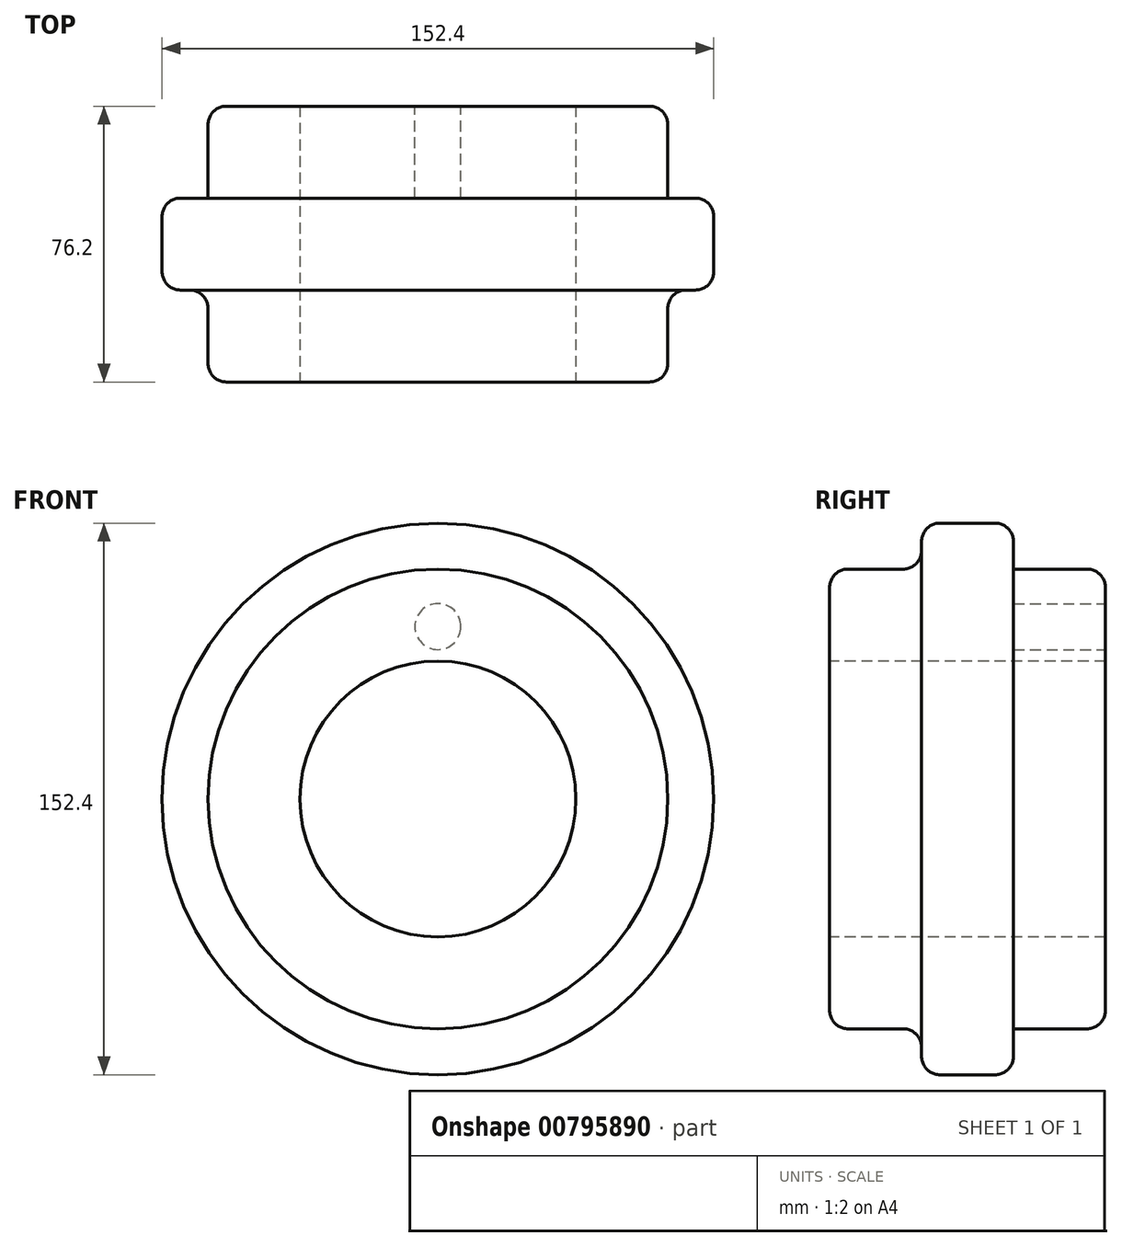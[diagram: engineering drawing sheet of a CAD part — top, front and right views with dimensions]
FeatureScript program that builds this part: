
annotation { "Feature Type Name" : "Feature", "Feature Type Description" : "" }
export const myFeature = defineFeature(function(context is Context, id is Id, definition is map)
    precondition{}
    {
        {
            var Q0;
            Q0=qCreatedBy(makeId("Right.planeOp"),FACE);
            var sketch = newSketch(context, id + "F0", { "sketchPlane" : qUnion([Q0])});
            skLineSegment(sketch, "E0", {"start": v(-38.1, 38.1) * mm, "end": v(38.1, 38.1) * mm});
            skLineSegment(sketch, "E1", {"start": v(38.1, 38.1) * mm, "end": v(38.1, 63.5) * mm});
            skLineSegment(sketch, "E2", {"start": v(38.1, 63.5) * mm, "end": v(12.7, 63.5) * mm});
            skLineSegment(sketch, "E3", {"start": v(12.7, 63.5) * mm, "end": v(12.7, 76.2) * mm});
            skLineSegment(sketch, "E4", {"start": v(12.7, 76.2) * mm, "end": v(-12.7, 76.2) * mm});
            skLineSegment(sketch, "E5", {"start": v(-12.7, 76.2) * mm, "end": v(-12.7, 63.5) * mm});
            skLineSegment(sketch, "E6", {"start": v(-12.7, 63.5) * mm, "end": v(-38.1, 63.5) * mm});
            skLineSegment(sketch, "E7", {"start": v(-38.1, 63.5) * mm, "end": v(-38.1, 38.1) * mm});
            skLineSegment(sketch, "E8", {"start": v(-68.16, 0) * mm, "end": v(78.02, 0) * mm, "construction": true});
            skLineSegment(sketch, "E9.bottom", {"start": v(-38.1, 38.1) * mm, "end": v(-16.51, 38.1) * mm});
            skLineSegment(sketch, "E9.top", {"start": v(-38.1, 25.4) * mm, "end": v(-16.51, 25.4) * mm});
            skLineSegment(sketch, "E9.left", {"start": v(-38.1, 38.1) * mm, "end": v(-38.1, 25.4) * mm});
            skLineSegment(sketch, "E9.right", {"start": v(-16.51, 38.1) * mm, "end": v(-16.51, 25.4) * mm});
            skSolve(sketch);
        }
        {
            var Q0;
            Q0=makeQuery(id+"F0.imprint","IMPRINT",FACE,{"disambiguationData":[TD([[makeQuery(id+"F0.imprint","IMPRINT",EDGE,{"derivedFrom":sQuery(id+"F0.wireOp",EDGE,"E0")}),1.0]])]});
            var Q1;
            Q1=makeQuery(id+"F0.imprint","IMPRINT",FACE,{"disambiguationData":[TD([[makeQuery(id+"F0.imprint","IMPRINT",EDGE,{"derivedFrom":sQuery(id+"F0.wireOp",EDGE,"E9.bottom")}),-1.0]])]});
            var Q2;
            Q2=sQuery(id+"F0.wireOp",EDGE,"E8");
            revolve(context, id + "F1", {"surfaceOperationType" : NewSurfaceOperationType.NEW, "entities" : qUnion([Q0, Q1]), "axis" : qUnion([Q2]), "revolveType" : RevolveType.FULL});
        }
        {
            var Q0;
            Q0=makeQuery(id+"F1.opRevolve","SWEPT_EDGE",EDGE,{"disambiguationData":[OSD([sQuery(id+"F0.wireOp",EDGE,"E5"),sQuery(id+"F0.wireOp",EDGE,"E6")])]});
            var Q1;
            Q1=makeQuery(id+"F1.opRevolve","SWEPT_EDGE",EDGE,{"disambiguationData":[OSD([sQuery(id+"F0.wireOp",EDGE,"E4"),sQuery(id+"F0.wireOp",EDGE,"E5")])]});
            var Q2;
            Q2=makeQuery(id+"F1.opRevolve","SWEPT_EDGE",EDGE,{"disambiguationData":[OSD([sQuery(id+"F0.wireOp",EDGE,"E3"),sQuery(id+"F0.wireOp",EDGE,"E4")])]});
            var Q3;
            Q3=makeQuery(id+"F1.opRevolve","SWEPT_EDGE",EDGE,{"disambiguationData":[OSD([sQuery(id+"F0.wireOp",EDGE,"E1"),sQuery(id+"F0.wireOp",EDGE,"E2")])]});
            var Q4;
            Q4=makeQuery(id+"F1.opRevolve","SWEPT_EDGE",EDGE,{"disambiguationData":[OSD([sQuery(id+"F0.wireOp",EDGE,"E6"),sQuery(id+"F0.wireOp",EDGE,"E7")])]});
            fillet(context, id + "F2", {"entities" : qUnion([Q0, Q1, Q2, Q3, Q4]), "radius" : 5.08 * mm, "tangentPropagation" : true, "allowEdgeOverflow" : false});
        }
        {
            var Q0;
            Q0=makeQuery(id+"F1.opRevolve","SWEPT_FACE",FACE,{"disambiguationData":[OSD([sQuery(id+"F0.wireOp",EDGE,"E1")])]});
            var sketch = newSketch(context, id + "F3", { "sketchPlane" : qUnion([Q0])});
            skCircle(sketch, "E10", {"center": v(0, 0) * mm, "radius": 47.63 * mm, "construction": true});
            skCircle(sketch, "E11", {"center": v(0, 47.63) * mm, "radius": 6.35 * mm});
            skSolve(sketch);
        }
        {
            var Q0;
            Q0=makeQuery(id+"F3.imprint","IMPRINT",FACE,{"disambiguationData":[TD([[makeQuery(id+"F3.imprint","IMPRINT",EDGE,{"derivedFrom":sQuery(id+"F3.wireOp",EDGE,"E11")}),1.0]])]});
            extrude(context, id + "F4", {"entities" : qUnion([Q0]), "operationType" : NewBodyOperationType.REMOVE, "oppositeDirection" : true, "depth" : 25.4 * mm, "offsetDistance" : 25.4 * mm});
        }
        {
            var Q0;
            Q0=qCreatedBy(makeId("Top.planeOp"),FACE);
            var sketch = newSketch(context, id + "F5", { "sketchPlane" : qUnion([Q0])});
            skLineSegment(sketch, "E12", {"start": v(0, 68.46) * mm, "end": v(0, -80.8) * mm, "construction": true});
            skSolve(sketch);
        }
    });
